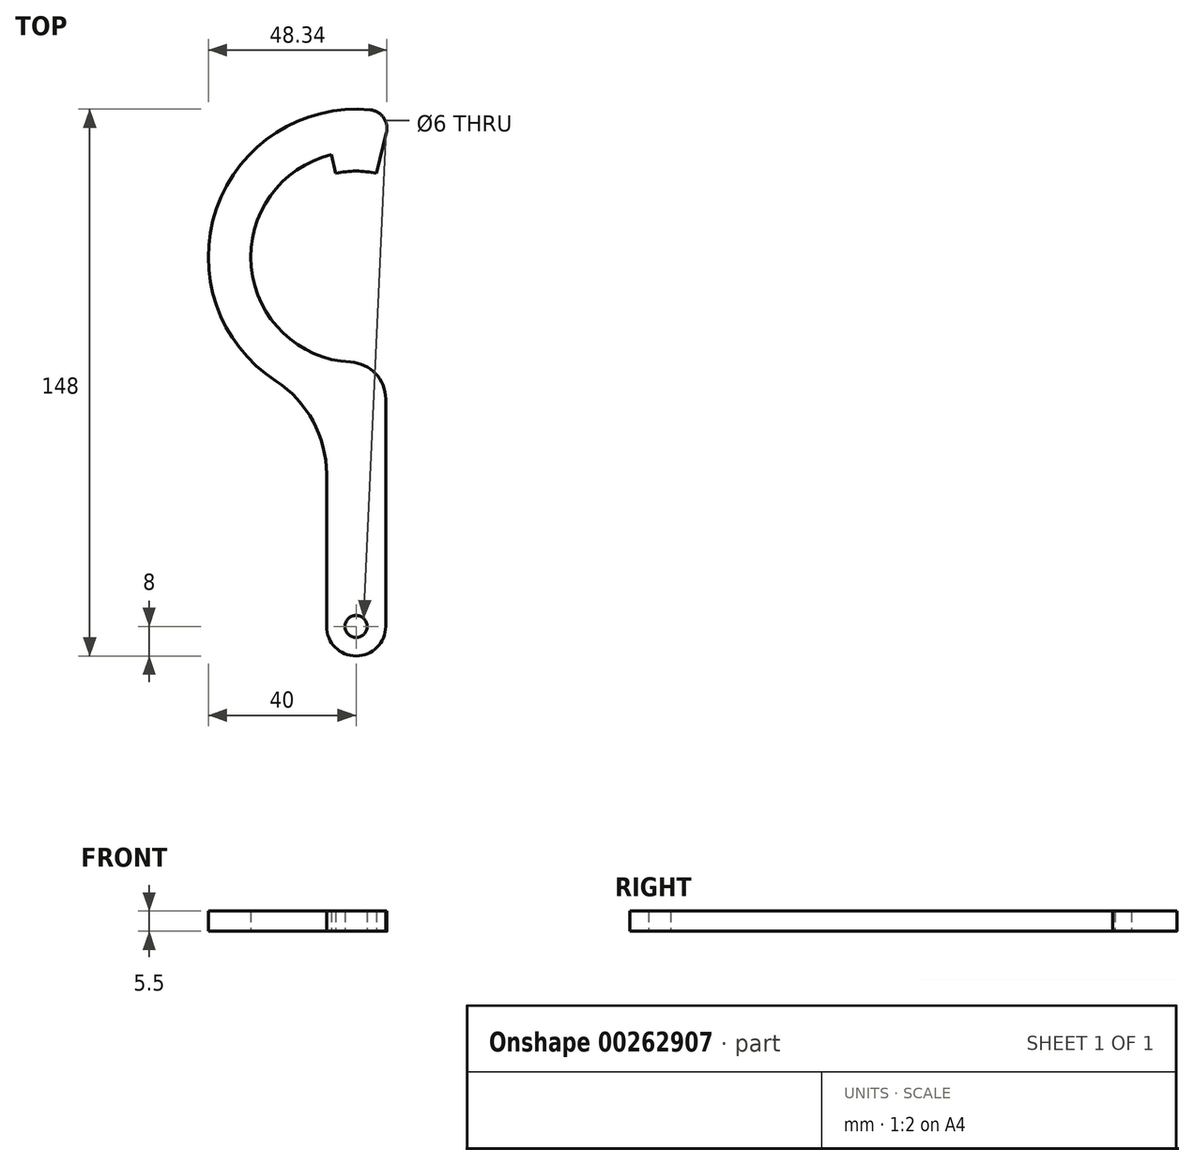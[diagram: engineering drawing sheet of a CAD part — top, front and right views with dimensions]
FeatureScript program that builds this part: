
annotation { "Feature Type Name" : "Feature", "Feature Type Description" : "" }
export const myFeature = defineFeature(function(context is Context, id is Id, definition is map)
    precondition{}
    {
        {
            var Q0;
            Q0=qCreatedBy(makeId("Top.planeOp"),FACE);
            var sketch = newSketch(context, id + "F0", { "sketchPlane" : qUnion([Q0])});
            skArc(sketch, "E0", {"start": v(-8, -100) * mm, "mid": v(0, -108) * mm, "end": v(8, -100) * mm});
            skLineSegment(sketch, "E1.trimOffspring", {"start": v(8, -38.45) * mm, "end": v(8, -100) * mm});
            skLineSegment(sketch, "E2.trimOffspring", {"start": v(-8, -58.79) * mm, "end": v(-8, -100) * mm});
            skCircle(sketch, "E3", {"center": v(0, -100) * mm, "radius": 3 * mm});
            skArc(sketch, "E4", {"start": v(-21.71, -33.6) * mm, "mid": v(36.74, -15.8) * mm, "end": v(9.46, 38.86) * mm, "construction": true});
            skLineSegment(sketch, "E5", {"start": v(0, 0) * mm, "end": v(0, -100) * mm, "construction": true});
            skLineSegment(sketch, "E6", {"start": v(-13.95, 37.49) * mm, "end": v(-13.95, 37.49) * mm});
            skLineSegment(sketch, "E7", {"start": v(32.13, 23.82) * mm, "end": v(32.13, 23.82) * mm});
            skArc(sketch, "E8.filletArc", {"start": v(-8, -58.79) * mm, "mid": v(-11.65, -44.45) * mm, "end": v(-21.71, -33.6) * mm});
            skPoint(sketch, "E9", {"position": v(0, 23.25) * mm});
            skPoint(sketch, "E10.1.0", {"position": v(-20.14, 11.63) * mm});
            skPoint(sketch, "E10.2.0", {"position": v(-20.14, -11.62) * mm});
            skPoint(sketch, "E10.3.0", {"position": v(0, -23.25) * mm});
            skPoint(sketch, "E10.4.0", {"position": v(20.14, -11.63) * mm});
            skPoint(sketch, "E10.5.0", {"position": v(20.14, 11.63) * mm});
            skLineSegment(sketch, "E11", {"start": v(5.5, 22.6) * mm, "end": v(8.2, 33.66) * mm});
            skLineSegment(sketch, "E12", {"start": v(-5.5, 22.6) * mm, "end": v(-6.74, 27.7) * mm});
            skPoint(sketch, "E13", {"position": v(-5.5, 22.6) * mm});
            skPoint(sketch, "E14", {"position": v(5.5, 22.6) * mm});
            skPoint(sketch, "E15", {"position": v(15.27, 17.53) * mm});
            skArc(sketch, "E16", {"start": v(6.74, 27.7) * mm, "mid": v(0, 28.5) * mm, "end": v(-6.74, 27.7) * mm, "construction": true});
            skArc(sketch, "E17", {"start": v(8, -27.35) * mm, "mid": v(30.26, 0.7) * mm, "end": v(6.74, 27.7) * mm, "construction": true});
            skPoint(sketch, "E18.visualSharp", {"position": v(8, -27.35) * mm});
            skArc(sketch, "E18.filletArc", {"start": v(8, -38.45) * mm, "mid": v(5.25, -31.56) * mm, "end": v(-1.48, -28.46) * mm});
            skArc(sketch, "E19", {"start": v(3.81, 39.82) * mm, "mid": v(-37.78, 13.14) * mm, "end": v(-21.71, -33.6) * mm});
            skArc(sketch, "E20", {"start": v(-6.74, 27.7) * mm, "mid": v(-28.38, -2.66) * mm, "end": v(-1.48, -28.46) * mm});
            skLineSegment(sketch, "E21", {"start": v(6.74, 27.7) * mm, "end": v(6.74, 27.7) * mm});
            skArc(sketch, "E22", {"start": v(5.5, 22.6) * mm, "mid": v(0, 23.25) * mm, "end": v(-5.5, 22.6) * mm});
            skArc(sketch, "E23", {"start": v(-5.5, 22.6) * mm, "mid": v(0, -23.25) * mm, "end": v(5.5, 22.6) * mm, "construction": true});
            skPoint(sketch, "E24.visualSharp", {"position": v(9.46, 38.86) * mm});
            skArc(sketch, "E24.filletArc", {"start": v(8.2, 33.66) * mm, "mid": v(7.41, 37.74) * mm, "end": v(3.81, 39.82) * mm});
            skSolve(sketch);
        }
        {
            var Q0;
            Q0=qSketchRegion(id+"F0",true);
            extrude(context, id + "F1", {"entities" : qUnion([Q0]), "depth" : 5.5 * mm});
        }
    });
